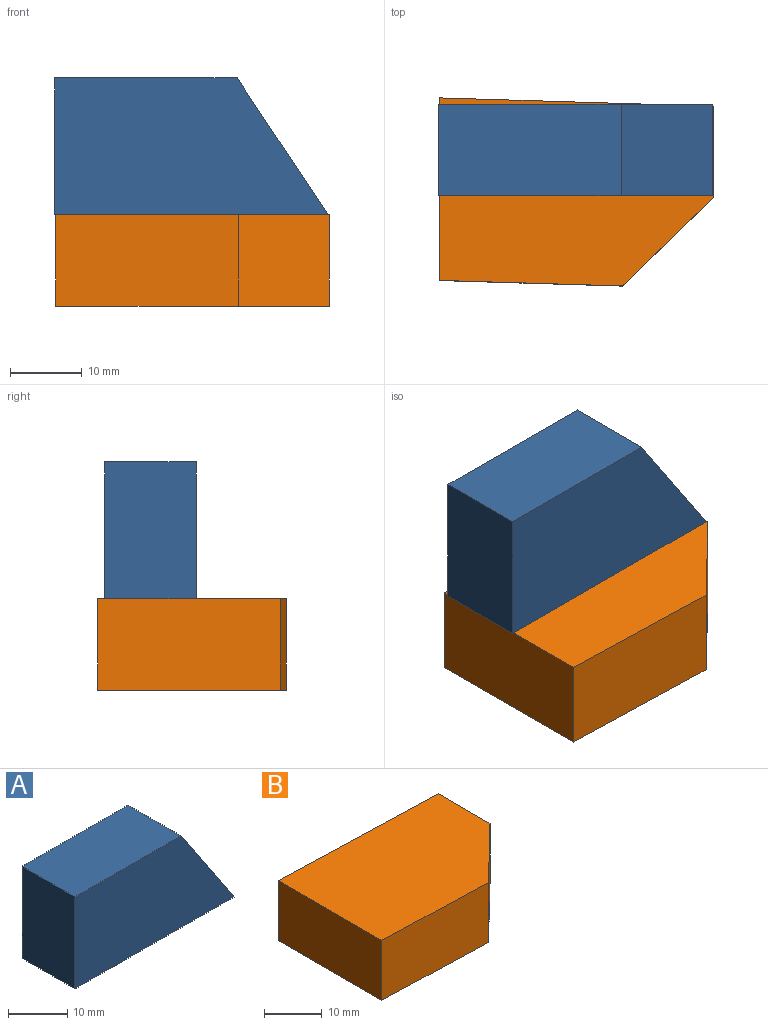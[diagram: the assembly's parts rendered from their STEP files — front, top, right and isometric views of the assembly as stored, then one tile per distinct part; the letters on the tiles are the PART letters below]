
ASSEMBLY  parts=2 mates=1
PART A: 6 faces, bbox 38.1x12.7x19.1 mm
  f0: plane 38.1x19.05mm, normal (0,-1,0), area 604.8mm2, adj f2,f3,f4,f5
  f1: plane 38.1x19.05mm, normal (0,1,0), area 604.8mm2, adj f2,f3,f4,f5
  f2: plane 19.05x12.7mm, normal (-1,0,0), area 241.9mm2, adj f0,f1,f3,f4
  f3: plane 38.1x12.7mm, normal (0,0,-1), area 483.9mm2, adj f0,f1,f2,f5
  f4: plane 25.4x12.7mm, normal (0,0,1), area 322.6mm2, adj f0,f1,f2,f5
  f5: plane 19.05x12.7mm, normal (0.83,0,0.55), area 290.8mm2, adj f0,f1,f3,f4
PART B: 7 faces, bbox 38.1x26.2x12.7 mm
  f0: plane 12.7x12.7mm, normal (1,0,0), area 161.3mm2, adj f1,f4,f5,f6
  f1: plane 38.08x12.7mm, normal (0.03,1,0), area 483.9mm2, adj f0,f2,f4,f5
  f2: plane 25.4x12.7mm, normal (-1,0,0), area 322.6mm2, adj f1,f3,f4,f5
  f3: plane 25.39x12.7mm, normal (-0.03,-1,0), area 322.6mm2, adj f2,f4,f5,f6
  f4: plane 38.08x26.17mm, normal (0,0,1), area 886.7mm2, adj f0,f1,f2,f3,f6
  f5: plane 38.08x26.17mm, normal (0,0,-1), area 886.7mm2, adj f0,f1,f2,f3,f6
  f6: plane 12.7x12.69mm, normal (0.7,-0.72,0), area 224.6mm2, adj f0,f3,f4,f5
PLACE A t=(-3.4,-40.8,21.65)mm
PLACE B t=(-3.24,-66.41,8.95)mm
MATE planar B.f4 <-> A.f3  axis (0,0,1) through (-22.29,-40.43,21.65)mm
